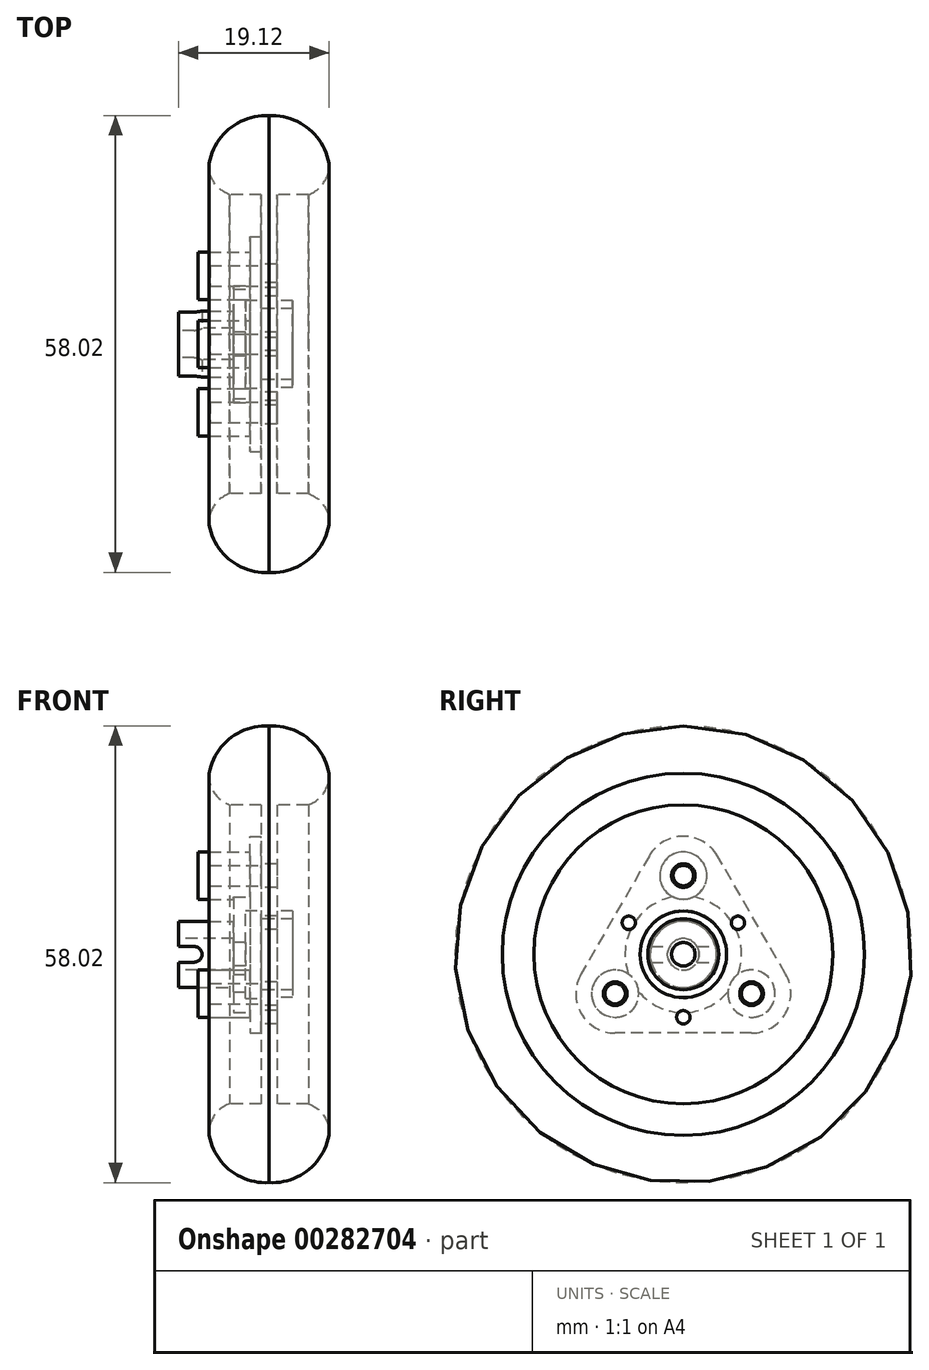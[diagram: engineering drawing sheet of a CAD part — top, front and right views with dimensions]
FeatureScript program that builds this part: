
annotation { "Feature Type Name" : "Feature", "Feature Type Description" : "" }
export const myFeature = defineFeature(function(context is Context, id is Id, definition is map)
    precondition{}
    {
        {
            var Q0;
            Q0=qCreatedBy(makeId("Front.planeOp"),FACE);
            var sketch = newSketch(context, id + "F0", { "sketchPlane" : qUnion([Q0])});
            skCircle(sketch, "E0", {"center": v(0, 0) * mm, "radius": 4.5 * mm, "construction": true});
            skCircle(sketch, "E1", {"center": v(0, 0) * mm, "radius": 5.5 * mm, "construction": true});
            skCircle(sketch, "E2", {"center": v(0, 0) * mm, "radius": 19 * mm, "construction": true});
            skCircle(sketch, "E3", {"center": v(0, 0) * mm, "radius": 23 * mm, "construction": true});
            skCircle(sketch, "E4", {"center": v(0, 0) * mm, "radius": 29 * mm, "construction": true});
            skLineSegment(sketch, "E5.bottom", {"start": v(0, 4.5) * mm, "end": v(1, 4.5) * mm});
            skLineSegment(sketch, "E5.left", {"start": v(0, 4.5) * mm, "end": v(0, 19) * mm});
            skLineSegment(sketch, "E5.right", {"start": v(1, 4.5) * mm, "end": v(1, 19) * mm});
            skLineSegment(sketch, "E6.bottom", {"start": v(0, 4.5) * mm, "end": v(3, 4.5) * mm});
            skLineSegment(sketch, "E6.top", {"start": v(0, 5.5) * mm, "end": v(3, 5.5) * mm});
            skLineSegment(sketch, "E6.left", {"start": v(0, 4.5) * mm, "end": v(0, 5.5) * mm});
            skLineSegment(sketch, "E6.right", {"start": v(3, 4.5) * mm, "end": v(3, 5.5) * mm});
            skLineSegment(sketch, "E7.bottom", {"start": v(0, 23) * mm, "end": v(5, 23) * mm});
            skLineSegment(sketch, "E7.top", {"start": v(0, 19) * mm, "end": v(5, 19) * mm});
            skLineSegment(sketch, "E7.left", {"start": v(0, 23) * mm, "end": v(0, 19) * mm});
            skLineSegment(sketch, "E7.right", {"start": v(5, 23) * mm, "end": v(5, 19) * mm});
            skCircle(sketch, "E8", {"center": v(0, 23) * mm, "radius": 7.6 * mm, "construction": true});
            skArc(sketch, "E9", {"start": v(5, 19) * mm, "mid": v(7, 20.55) * mm, "end": v(7.6, 23) * mm});
            skArc(sketch, "E10", {"start": v(7.6, 23) * mm, "mid": v(4.94, 27.44) * mm, "end": v(0, 29) * mm});
            skLineSegment(sketch, "E11.MirrorCS", {"start": v(0, 4.5) * mm, "end": v(-1, 4.5) * mm});
            skLineSegment(sketch, "E12.MirrorCS", {"start": v(0, 5.5) * mm, "end": v(-3, 5.5) * mm});
            skLineSegment(sketch, "E13.MirrorCS", {"start": v(-3, 4.5) * mm, "end": v(-3, 5.5) * mm});
            skLineSegment(sketch, "E14.MirrorCS", {"start": v(0, 4.5) * mm, "end": v(-3, 4.5) * mm});
            skLineSegment(sketch, "E15.MirrorCS", {"start": v(0, 19) * mm, "end": v(-5, 19) * mm});
            skArc(sketch, "E16.MirrorCS", {"start": v(-5, 19) * mm, "mid": v(-7, 20.55) * mm, "end": v(-7.6, 23) * mm});
            skLineSegment(sketch, "E17.MirrorCS", {"start": v(-5, 23) * mm, "end": v(-5, 19) * mm});
            skArc(sketch, "E18.MirrorCS", {"start": v(-7.6, 23) * mm, "mid": v(-4.94, 27.44) * mm, "end": v(0, 29) * mm});
            skLineSegment(sketch, "E19.MirrorCS", {"start": v(-1, 4.5) * mm, "end": v(-1, 19) * mm});
            skLineSegment(sketch, "E20.MirrorCS", {"start": v(0, 23) * mm, "end": v(-5, 23) * mm});
            skSolve(sketch);
        }
        {
            var Q0;
            Q0=qCreatedBy(makeId("Front.planeOp"),FACE);
            var sketch = newSketch(context, id + "F1", { "sketchPlane" : qUnion([Q0])});
            skLineSegment(sketch, "E21", {"start": v(-37.16, 0) * mm, "end": v(45.3, 0) * mm, "construction": true});
            skSolve(sketch);
        }
        {
            var Q0;
            Q0=qSketchRegion(id+"F0",true);
            var Q1;
            Q1=sQuery(id+"F1.wireOp",EDGE,"E21");
            revolve(context, id + "F2", {"entities" : qUnion([Q0]), "axis" : qUnion([Q1]), "revolveType" : RevolveType.FULL});
        }
        {
            var Q0;
            Q0=makeQuery(id+"F2.opRevolve","SWEPT_FACE",FACE,{"disambiguationData":[OSD([sQuery(id+"F0.wireOp",EDGE,"E19.MirrorCS")])]});
            var sketch = newSketch(context, id + "F3", { "sketchPlane" : qUnion([Q0])});
            skCircle(sketch, "E22", {"center": v(0, 0) * mm, "radius": 10 * mm, "construction": true});
            skCircle(sketch, "E23", {"center": v(0, 10) * mm, "radius": 1.5 * mm});
            skCircle(sketch, "E24.1.0", {"center": v(-8.66, -5) * mm, "radius": 1.5 * mm});
            skCircle(sketch, "E24.2.0", {"center": v(8.66, -5) * mm, "radius": 1.5 * mm});
            skCircle(sketch, "E25", {"center": v(0, 0) * mm, "radius": 8 * mm, "construction": true});
            skCircle(sketch, "E26", {"center": v(0, -8) * mm, "radius": 0.85 * mm});
            skCircle(sketch, "E27.1.0", {"center": v(6.93, 4) * mm, "radius": 0.85 * mm});
            skCircle(sketch, "E27.2.0", {"center": v(-6.93, 4) * mm, "radius": 0.85 * mm});
            skSolve(sketch);
        }
        {
            var Q0;
            Q0=qSketchRegion(id+"F3",true);
            extrude(context, id + "F4", {"entities" : qUnion([Q0]), "operationType" : NewBodyOperationType.REMOVE, "endBound" : BoundingType.THROUGH_ALL, "oppositeDirection" : true, "depth" : 25 * mm});
        }
        {
            var Q0;
            Q0=makeQuery(id+"F2.opRevolve","SWEPT_FACE",FACE,{"disambiguationData":[OSD([sQuery(id+"F0.wireOp",EDGE,"E19.MirrorCS")])]});
            var sketch = newSketch(context, id + "F5", { "sketchPlane" : qUnion([Q0])});
            skLineSegment(sketch, "E28", {"start": v(0, 10) * mm, "end": v(-8.66, -5) * mm, "construction": true});
            skLineSegment(sketch, "E29", {"start": v(-8.66, -5) * mm, "end": v(8.66, -5) * mm, "construction": true});
            skLineSegment(sketch, "E30", {"start": v(8.66, -5) * mm, "end": v(0, 10) * mm, "construction": true});
            skLineSegment(sketch, "E31", {"start": v(-14.43, -5) * mm, "end": v(-3.32, 14.25) * mm, "construction": true});
            skLineSegment(sketch, "E32", {"start": v(2.44, 15.78) * mm, "end": v(14.43, -5) * mm, "construction": true});
            skLineSegment(sketch, "E33", {"start": v(-13.1, -10) * mm, "end": v(12.36, -10) * mm, "construction": true});
            skCircle(sketch, "E34", {"center": v(0, 10) * mm, "radius": 5 * mm});
            skCircle(sketch, "E35", {"center": v(-8.66, -5) * mm, "radius": 5 * mm});
            skCircle(sketch, "E36", {"center": v(8.66, -5) * mm, "radius": 5 * mm});
            skLineSegment(sketch, "E37", {"start": v(-13, -2.5) * mm, "end": v(-4.33, 12.5) * mm});
            skLineSegment(sketch, "E38", {"start": v(4.33, 12.5) * mm, "end": v(13, -2.5) * mm});
            skLineSegment(sketch, "E39", {"start": v(-8.66, -10) * mm, "end": v(8.66, -10) * mm});
            skSolve(sketch);
        }
        {
            var Q0;
            Q0=qSketchRegion(id+"F5",true);
            extrude(context, id + "F6", {"entities" : qUnion([Q0]), "depth" : 1.4 * mm});
        }
        {
            var Q0;
            Q0=makeQuery(id+"F6.opExtrude","CAP_FACE",FACE,{"disambiguationData":[OSD([sQuery(id+"F5.wireOp",EDGE,"E34"),sQuery(id+"F5.wireOp",EDGE,"E35"),sQuery(id+"F5.wireOp",EDGE,"E36"),sQuery(id+"F5.wireOp",EDGE,"E37"),sQuery(id+"F5.wireOp",EDGE,"E38"),sQuery(id+"F5.wireOp",EDGE,"E39")])],"isStart":true});
            var sketch = newSketch(context, id + "F7", { "sketchPlane" : qUnion([Q0])});
            skCircle(sketch, "E40", {"center": v(0, 10) * mm, "radius": 3 * mm});
            skCircle(sketch, "E41.1.0", {"center": v(-8.66, -5) * mm, "radius": 3 * mm});
            skCircle(sketch, "E41.2.0", {"center": v(8.66, -5) * mm, "radius": 3 * mm});
            skPoint(sketch, "E41.center", {"position": v(0, 0) * mm});
            skSolve(sketch);
        }
        {
            var Q0;
            Q0=qSketchRegion(id+"F7",true);
            extrude(context, id + "F8", {"entities" : qUnion([Q0]), "operationType" : NewBodyOperationType.ADD, "oppositeDirection" : true, "depth" : 8 * mm});
        }
        {
            var Q0;
            Q0=makeQuery(id+"F6.opExtrude","CAP_FACE",FACE,{"disambiguationData":[OSD([sQuery(id+"F5.wireOp",EDGE,"E34"),sQuery(id+"F5.wireOp",EDGE,"E35"),sQuery(id+"F5.wireOp",EDGE,"E36"),sQuery(id+"F5.wireOp",EDGE,"E37"),sQuery(id+"F5.wireOp",EDGE,"E38"),sQuery(id+"F5.wireOp",EDGE,"E39")])],"isStart":true});
            var sketch = newSketch(context, id + "F9", { "sketchPlane" : qUnion([Q0])});
            skCircle(sketch, "E42", {"center": v(0, 0) * mm, "radius": 4.2 * mm});
            skSolve(sketch);
        }
        {
            var Q0;
            Q0=qSketchRegion(id+"F9",true);
            extrude(context, id + "F10", {"entities" : qUnion([Q0]), "operationType" : NewBodyOperationType.ADD, "oppositeDirection" : true, "depth" : 10.5 * mm});
        }
        {
            var Q0;
            Q0=makeQuery(id+"F6.opExtrude","CAP_FACE",FACE,{"disambiguationData":[OSD([sQuery(id+"F5.wireOp",EDGE,"E34"),sQuery(id+"F5.wireOp",EDGE,"E35"),sQuery(id+"F5.wireOp",EDGE,"E36"),sQuery(id+"F5.wireOp",EDGE,"E37"),sQuery(id+"F5.wireOp",EDGE,"E38"),sQuery(id+"F5.wireOp",EDGE,"E39")])],"isStart":true});
            var sketch = newSketch(context, id + "F11", { "sketchPlane" : qUnion([Q0])});
            skCircle(sketch, "E43", {"center": v(0, 0) * mm, "radius": 7.4 * mm});
            skSolve(sketch);
        }
        {
            var Q0;
            Q0=qSketchRegion(id+"F11",true);
            extrude(context, id + "F12", {"entities" : qUnion([Q0]), "operationType" : NewBodyOperationType.ADD, "oppositeDirection" : true, "depth" : 3.5 * mm});
        }
        {
            var Q0;
            Q0=makeQuery(id+"F6.opExtrude","CAP_FACE",FACE,{"disambiguationData":[OSD([sQuery(id+"F5.wireOp",EDGE,"E34"),sQuery(id+"F5.wireOp",EDGE,"E35"),sQuery(id+"F5.wireOp",EDGE,"E36"),sQuery(id+"F5.wireOp",EDGE,"E37"),sQuery(id+"F5.wireOp",EDGE,"E38"),sQuery(id+"F5.wireOp",EDGE,"E39")])],"isStart":true});
            var sketch = newSketch(context, id + "F13", { "sketchPlane" : qUnion([Q0])});
            skCircle(sketch, "E44", {"center": v(0, 0) * mm, "radius": 5.6 * mm});
            skSolve(sketch);
        }
        {
            var Q0;
            Q0=qSketchRegion(id+"F13",true);
            extrude(context, id + "F14", {"entities" : qUnion([Q0]), "operationType" : NewBodyOperationType.REMOVE, "oppositeDirection" : true, "depth" : 2 * mm});
        }
        {
            var Q0;
            Q0=makeQuery(id+"F10.opExtrude","CAP_FACE",FACE,{"disambiguationData":[OSD([sQuery(id+"F9.wireOp",EDGE,"E42")])],"isStart":false});
            var sketch = newSketch(context, id + "F15", { "sketchPlane" : qUnion([Q0])});
            skCircle(sketch, "E45", {"center": v(0, 0) * mm, "radius": 1.5 * mm});
            skSolve(sketch);
        }
        {
            var Q0;
            Q0=qSketchRegion(id+"F15",true);
            extrude(context, id + "F16", {"entities" : qUnion([Q0]), "operationType" : NewBodyOperationType.REMOVE, "endBound" : BoundingType.THROUGH_ALL, "oppositeDirection" : true, "depth" : 25 * mm});
        }
        {
            var Q0;
            Q0=makeQuery(id+"F10.opExtrude","CAP_FACE",FACE,{"disambiguationData":[OSD([sQuery(id+"F9.wireOp",EDGE,"E42")])],"isStart":false});
            var sketch = newSketch(context, id + "F17", { "sketchPlane" : qUnion([Q0])});
            skCircle(sketch, "E46", {"center": v(0, 0) * mm, "radius": 2 * mm});
            skSolve(sketch);
        }
        {
            var Q0;
            Q0=qSketchRegion(id+"F17",true);
            extrude(context, id + "F18", {"entities" : qUnion([Q0]), "operationType" : NewBodyOperationType.REMOVE, "oppositeDirection" : true, "depth" : 7 * mm});
        }
        {
            var Q0;
            Q0=makeQuery(id+"F6.opExtrude","CAP_FACE",FACE,{"disambiguationData":[OSD([sQuery(id+"F5.wireOp",EDGE,"E34"),sQuery(id+"F5.wireOp",EDGE,"E35"),sQuery(id+"F5.wireOp",EDGE,"E36"),sQuery(id+"F5.wireOp",EDGE,"E37"),sQuery(id+"F5.wireOp",EDGE,"E38"),sQuery(id+"F5.wireOp",EDGE,"E39")])],"isStart":true});
            var sketch = newSketch(context, id + "F19", { "sketchPlane" : qUnion([Q0])});
            skCircle(sketch, "E47", {"center": v(0, 10) * mm, "radius": 1.3 * mm});
            skCircle(sketch, "E48.1.0", {"center": v(-8.66, -5) * mm, "radius": 1.3 * mm});
            skCircle(sketch, "E48.2.0", {"center": v(8.66, -5) * mm, "radius": 1.3 * mm});
            skPoint(sketch, "E48.center", {"position": v(0, 0) * mm});
            skSolve(sketch);
        }
        {
            var Q0;
            Q0=qSketchRegion(id+"F19",true);
            extrude(context, id + "F20", {"entities" : qUnion([Q0]), "operationType" : NewBodyOperationType.REMOVE, "oppositeDirection" : true, "depth" : 6.5 * mm});
        }
        {
            var Q0;
            Q0=qCreatedBy(makeId("Front.planeOp"),FACE);
            var sketch = newSketch(context, id + "F21", { "sketchPlane" : qUnion([Q0])});
            skCircle(sketch, "E49", {"center": v(-11.5, 0) * mm, "radius": 1 * mm, "construction": true});
            skLineSegment(sketch, "E50.bottom", {"start": v(-11.5, -1) * mm, "end": v(-9.5, -1) * mm});
            skLineSegment(sketch, "E50.top", {"start": v(-11.5, 1) * mm, "end": v(-9.5, 1) * mm});
            skLineSegment(sketch, "E50.left", {"start": v(-11.5, -1) * mm, "end": v(-11.5, 1) * mm});
            skArc(sketch, "E51", {"start": v(-9.5, 1) * mm, "mid": v(-8.5, 0) * mm, "end": v(-9.5, -1) * mm});
            skSolve(sketch);
        }
        {
            var Q0;
            Q0=qSketchRegion(id+"F21",true);
            extrude(context, id + "F22", {"entities" : qUnion([Q0]), "operationType" : NewBodyOperationType.REMOVE, "oppositeDirection" : true, "depth" : 25 * mm, "hasSecondDirection" : true, "secondDirectionOppositeDirection" : false, "secondDirectionDepth" : 25 * mm});
        }
    });
